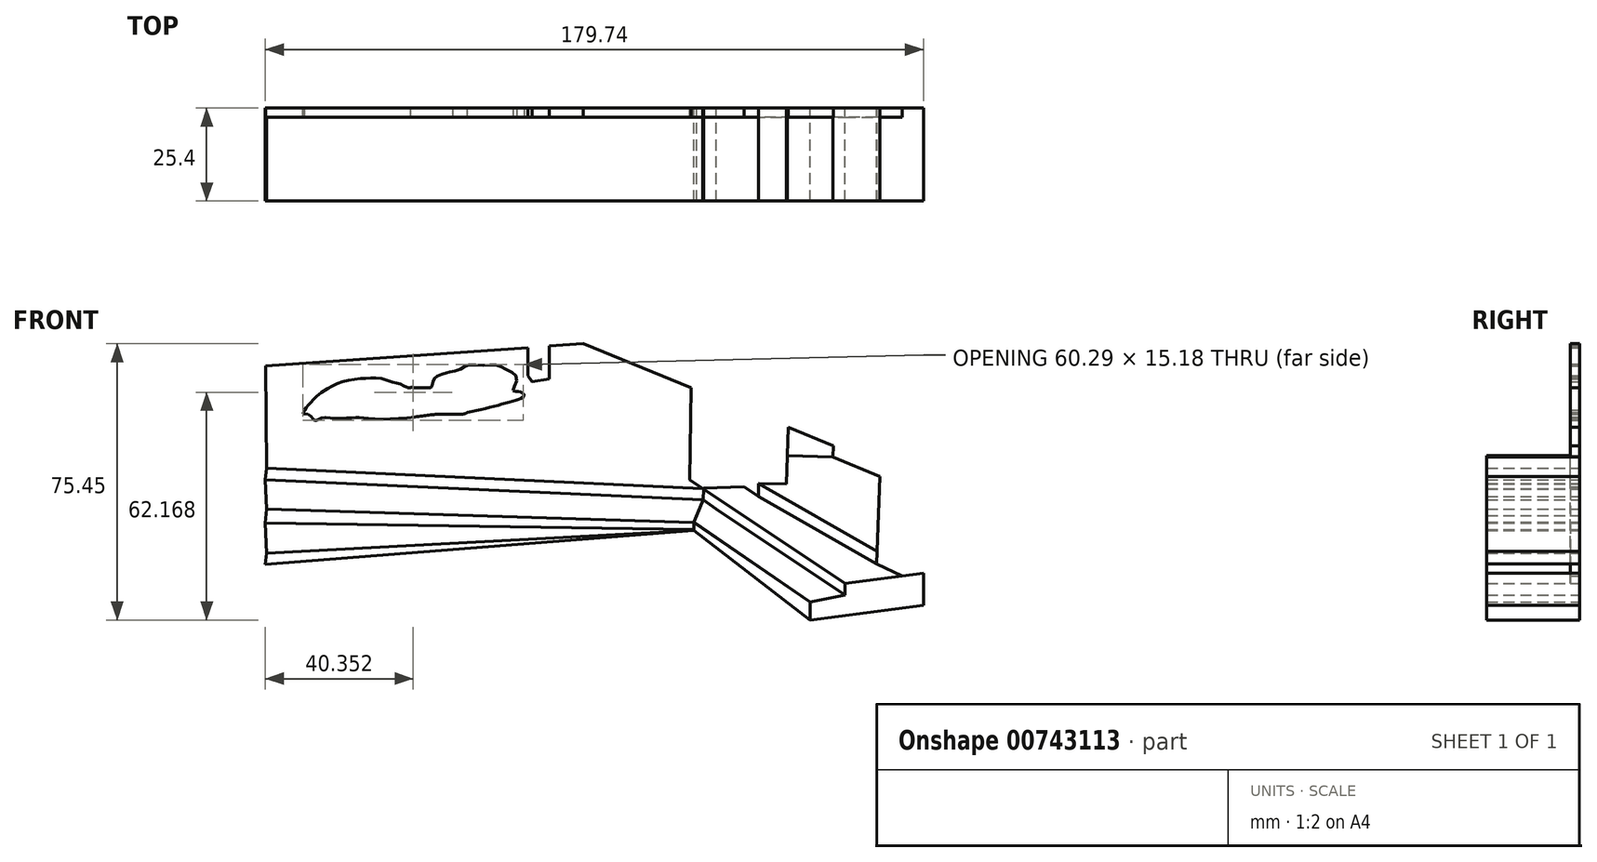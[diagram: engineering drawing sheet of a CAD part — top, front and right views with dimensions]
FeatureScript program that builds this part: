
annotation { "Feature Type Name" : "Feature", "Feature Type Description" : "" }
export const myFeature = defineFeature(function(context is Context, id is Id, definition is map)
    precondition{}
    {
        {
            var Q0;
            Q0=qCreatedBy(makeId("Front.planeOp"),FACE);
            var sketch = newSketch(context, id + "F0", { "sketchPlane" : qUnion([Q0])});
            skSolve(sketch);
        }
        {
            var Q0;
            Q0=qCreatedBy(makeId("Front.planeOp"),FACE);
            var sketch = newSketch(context, id + "F1", { "sketchPlane" : qUnion([Q0])});
            skPoint(sketch, "E0.0", {"position": v(-102.83, 77.74) * mm});
            skPoint(sketch, "E1.0", {"position": v(103.52, 77.74) * mm});
            skPoint(sketch, "E2.0", {"position": v(103.52, -77.03) * mm});
            skPoint(sketch, "E3.0", {"position": v(-102.83, -77.03) * mm});
            skLineSegment(sketch, "E4", {"start": v(-102.83, 77.74) * mm, "end": v(103.52, 77.74) * mm});
            skLineSegment(sketch, "E5", {"start": v(103.52, 77.74) * mm, "end": v(103.52, -77.03) * mm});
            skLineSegment(sketch, "E6", {"start": v(103.52, -77.03) * mm, "end": v(-102.83, -77.03) * mm});
            skLineSegment(sketch, "E7", {"start": v(-102.83, -77.03) * mm, "end": v(-102.83, 77.74) * mm});
            skLineSegment(sketch, "E8", {"start": v(43.21, -41.09) * mm, "end": v(82.08, -67.06) * mm});
            skLineSegment(sketch, "E9", {"start": v(82.08, -67.06) * mm, "end": v(97.77, -65) * mm});
            skLineSegment(sketch, "E10", {"start": v(97.77, -65) * mm, "end": v(103.52, 77.74) * mm});
            skLineSegment(sketch, "E11", {"start": v(97.77, -65) * mm, "end": v(90.72, -61.75) * mm});
            skLineSegment(sketch, "E12", {"start": v(90.72, -61.75) * mm, "end": v(96.33, 77.74) * mm});
            skLineSegment(sketch, "E13", {"start": v(95.01, 44.94) * mm, "end": v(60.47, 41.76) * mm});
            skLineSegment(sketch, "E14", {"start": v(60.47, 41.76) * mm, "end": v(58.42, -43.25) * mm});
            skLineSegment(sketch, "E15", {"start": v(66.15, -39.91) * mm, "end": v(68.3, 42.48) * mm});
            skLineSegment(sketch, "E16", {"start": v(68, 30.8) * mm, "end": v(80.72, 30.8) * mm});
            skLineSegment(sketch, "E17", {"start": v(80.72, 30.8) * mm, "end": v(78.77, -32.46) * mm});
            skLineSegment(sketch, "E18", {"start": v(78.77, -32.46) * mm, "end": v(87.41, -36.06) * mm});
            skLineSegment(sketch, "E19", {"start": v(87.41, -36.06) * mm, "end": v(89.94, 32.95) * mm});
            skLineSegment(sketch, "E20", {"start": v(89.94, 32.95) * mm, "end": v(94.53, 32.95) * mm});
            skLineSegment(sketch, "E21", {"start": v(50.64, -49.22) * mm, "end": v(82.08, -70.23) * mm});
            skLineSegment(sketch, "E22", {"start": v(82.08, -70.23) * mm, "end": v(82.08, -67.06) * mm});
            skLineSegment(sketch, "E23", {"start": v(50.64, -49.22) * mm, "end": v(46.93, -46.74) * mm});
            skLineSegment(sketch, "E24", {"start": v(45.9, 65.04) * mm, "end": v(43.36, -44.35) * mm});
            skLineSegment(sketch, "E25", {"start": v(43.21, -41.09) * mm, "end": v(54.51, -40.66) * mm});
            skLineSegment(sketch, "E26", {"start": v(54.51, -40.66) * mm, "end": v(58.42, -43.25) * mm});
            skLineSegment(sketch, "E27", {"start": v(54.51, -40.66) * mm, "end": v(57.06, 64.5) * mm});
            skLineSegment(sketch, "E28", {"start": v(45.9, 65.04) * mm, "end": v(57.06, 64.78) * mm});
            skLineSegment(sketch, "E29", {"start": v(57.06, 64.78) * mm, "end": v(57.06, 64.5) * mm});
            skLineSegment(sketch, "E30", {"start": v(57.06, 64.78) * mm, "end": v(102.77, 77.74) * mm});
            skLineSegment(sketch, "E31", {"start": v(97.77, -65) * mm, "end": v(103.52, -64.25) * mm});
            skLineSegment(sketch, "E32", {"start": v(43.13, -52.08) * mm, "end": v(43.13, -52.02) * mm});
            skLineSegment(sketch, "E33", {"start": v(82.08, -70.23) * mm, "end": v(73.38, -72.02) * mm});
            skLineSegment(sketch, "E34", {"start": v(58.5, -39.71) * mm, "end": v(90.86, -58.24) * mm});
            skLineSegment(sketch, "E35", {"start": v(58.5, -39.71) * mm, "end": v(66.15, -39.91) * mm});
            skLineSegment(sketch, "E36", {"start": v(43.21, -41.09) * mm, "end": v(39.7, -38.74) * mm});
            skLineSegment(sketch, "E37", {"start": v(39.7, -38.74) * mm, "end": v(40.84, 41.03) * mm});
            skLineSegment(sketch, "E38", {"start": v(40.84, 41.03) * mm, "end": v(-3.35, 35.9) * mm});
            skLineSegment(sketch, "E39", {"start": v(-3.35, 35.9) * mm, "end": v(-3.35, -11.94) * mm});
            skLineSegment(sketch, "E40", {"start": v(-3.35, -11.94) * mm, "end": v(1.34, -11.22) * mm});
            skLineSegment(sketch, "E41", {"start": v(1.34, -11.22) * mm, "end": v(1.34, 36.44) * mm});
            skLineSegment(sketch, "E42", {"start": v(-4.84, 49.27) * mm, "end": v(-4.49, -10.33) * mm});
            skLineSegment(sketch, "E43", {"start": v(-4.49, -10.33) * mm, "end": v(-3.35, -11.94) * mm});
            skLineSegment(sketch, "E44", {"start": v(1.34, 36.44) * mm, "end": v(25.15, 35.82) * mm});
            skLineSegment(sketch, "E45", {"start": v(25.15, 35.82) * mm, "end": v(25.15, 39.2) * mm});
            skLineSegment(sketch, "E46", {"start": v(-4.84, 49.27) * mm, "end": v(45.9, 65.04) * mm});
            skLineSegment(sketch, "E47", {"start": v(-75.94, -35.54) * mm, "end": v(-76.18, -7.57) * mm});
            skLineSegment(sketch, "E48", {"start": v(-76.18, -7.57) * mm, "end": v(-4.53, -2.63) * mm});
            skLineSegment(sketch, "E49.trimOffspring", {"start": v(1.34, -2.22) * mm, "end": v(10.65, -1.58) * mm});
            skLineSegment(sketch, "E50", {"start": v(43.21, -41.09) * mm, "end": v(-75.94, -35.54) * mm});
            skLineSegment(sketch, "E51", {"start": v(-75.94, -35.54) * mm, "end": v(-76.22, -38.74) * mm});
            skLineSegment(sketch, "E52", {"start": v(-76.22, -38.74) * mm, "end": v(43.21, -44.26) * mm});
            skLineSegment(sketch, "E53", {"start": v(40.83, -50.44) * mm, "end": v(-75.94, -46.74) * mm});
            skPoint(sketch, "E53.endSnap0", {"position": v(46.93, -46.74) * mm});
            skLineSegment(sketch, "E54", {"start": v(-75.94, -46.74) * mm, "end": v(-76.22, -50.51) * mm});
            skLineSegment(sketch, "E55", {"start": v(-76.22, -50.51) * mm, "end": v(40.83, -52.38) * mm});
            skLineSegment(sketch, "E56", {"start": v(40.83, -52.54) * mm, "end": v(-75.94, -58.86) * mm});
            skLineSegment(sketch, "E57", {"start": v(-75.94, -58.86) * mm, "end": v(-76.22, -61.88) * mm});
            skLineSegment(sketch, "E58", {"start": v(-76.22, -61.88) * mm, "end": v(40.83, -52.6) * mm});
            skLineSegment(sketch, "E59", {"start": v(-75.94, -58.86) * mm, "end": v(-76.22, -50.51) * mm});
            skLineSegment(sketch, "E60", {"start": v(-75.94, -46.74) * mm, "end": v(-76.22, -38.74) * mm});
            skLineSegment(sketch, "E61", {"start": v(-76.22, -61.88) * mm, "end": v(-76.22, -50.51) * mm});
            skLineSegment(sketch, "E62", {"start": v(-76.22, -38.74) * mm, "end": v(-76.22, -50.51) * mm});
            skLineSegment(sketch, "E63", {"start": v(-76.22, -38.74) * mm, "end": v(-76.45, -11.36) * mm});
            skLineSegment(sketch, "E64", {"start": v(-76.45, -11.36) * mm, "end": v(-76.18, -7.57) * mm});
            skLineSegment(sketch, "E65", {"start": v(90.72, -61.75) * mm, "end": v(58.42, -43.25) * mm});
            skLineSegment(sketch, "E66", {"start": v(87.41, -36.06) * mm, "end": v(91.68, -37.84) * mm});
            skLineSegment(sketch, "E67", {"start": v(103.52, -70.23) * mm, "end": v(103.52, -64.25) * mm});
            skLineSegment(sketch, "E68", {"start": v(17.54, 36.02) * mm, "end": v(17.54, -3.57) * mm});
            skLineSegment(sketch, "E69", {"start": v(17.54, -3.57) * mm, "end": v(40.07, -12.34) * mm});
            skLineSegment(sketch, "E70", {"start": v(78.77, -32.46) * mm, "end": v(66.36, -32.14) * mm});
            skLineSegment(sketch, "E71", {"start": v(78.86, -29.47) * mm, "end": v(66.56, -24.44) * mm});
            skLineSegment(sketch, "E72.trimOffspring", {"start": v(40.05, -13.6) * mm, "end": v(17.54, -4.4) * mm});
            skLineSegment(sketch, "E73.trimOffspring", {"start": v(66.6, -22.66) * mm, "end": v(78.92, -27.46) * mm});
            skLineSegment(sketch, "E74", {"start": v(17.54, -3.57) * mm, "end": v(17.54, -4.4) * mm});
            skLineSegment(sketch, "E75", {"start": v(17.54, -4.4) * mm, "end": v(10.65, -1.58) * mm});
            skFitSpline(sketch, "E76", {"points": [v(-66.01, -20.65) * mm, v(-65.13, -20.7) * mm, v(-63.54, -21.59) * mm, v(-62.6, -22.57) * mm, v(-60.78, -21.82) * mm, v(-57.56, -21.91) * mm, v(-52.75, -21.82) * mm, v(-50.41, -21.73) * mm, v(-45.84, -22.15) * mm, v(-35.4, -21.56) * mm, v(-29.46, -20.86) * mm, v(-23.95, -20.71) * mm, v(-17.04, -19.5) * mm, v(-10.69, -17.81) * mm, v(-6.95, -16.7) * mm, v(-5.55, -15.76) * mm, v(-6.2, -14.83) * mm, v(-7.89, -14.54) * mm, v(-8.54, -14.36) * mm, v(-7.7, -12.12) * mm, v(-8.17, -9.78) * mm, v(-9.94, -8.94) * mm, v(-10.6, -8.47) * mm, v(-13.21, -7.35) * mm, v(-16.85, -7.44) * mm, v(-21.34, -7.54) * mm, v(-22.83, -8.47) * mm, v(-25.64, -9.22) * mm, v(-26.94, -9.6) * mm, v(-29, -10.25) * mm, v(-30.21, -11.28) * mm, v(-30.5, -12.4) * mm, v(-30.87, -13.42) * mm, v(-30.96, -13.52) * mm, v(-31.8, -13.61) * mm, v(-33.3, -13.61) * mm, v(-35.07, -13.61) * mm, v(-35.91, -13.52) * mm, v(-36, -13.52) * mm, v(-36.47, -13.52) * mm], "startDerivative": vector(49.88, 3) * mm, "endDerivative": vector(-48.9, 0.35) * mm});
            skFitSpline(sketch, "E77", {"points": [v(-36.47, -13.52) * mm, v(-37.48, -13.52) * mm, v(-39.06, -12.71) * mm, v(-40.65, -12.3) * mm, v(-44.16, -11.17) * mm, v(-47.7, -10.98) * mm, v(-50.98, -11.17) * mm, v(-55.6, -12.1) * mm, v(-58.7, -13.52) * mm, v(-62.77, -16.39) * mm, v(-63.75, -17.6) * mm, v(-64.96, -18.77) * mm, v(-65.48, -19.7) * mm, v(-65.74, -20.64) * mm], "startDerivative": vector(-19.12, -3.26) * mm, "endDerivative": vector(-4.99, -19.18) * mm});
            skFitSpline(sketch, "E78", {"points": [v(-66.01, -20.65) * mm, v(-65.48, -19.7) * mm], "startDerivative": vector(0.54, 0.95) * mm, "endDerivative": vector(0.54, 0.95) * mm});
            skFitSpline(sketch, "E79", {"points": [v(-37.48, -13.52) * mm, v(-35.73, -14.13) * mm, v(-35.02, -14.6) * mm, v(-34.18, -15.67) * mm, v(-33.9, -16) * mm, v(-32.18, -17.35) * mm, v(-31.52, -18.05) * mm, v(-31.62, -19.13) * mm, v(-32.22, -20.06) * mm, v(-33.34, -20.86) * mm, v(-35.4, -21.56) * mm], "startDerivative": vector(16.47, -5.37) * mm, "endDerivative": vector(-16.95, -4.88) * mm});
            skFitSpline(sketch, "E80", {"points": [v(-29.46, -18.99) * mm, v(-27.64, -20.34) * mm, v(-24.93, -20.77) * mm, v(-21, -20.33) * mm, v(-19.66, -17.3) * mm, v(-19.24, -15.25) * mm, v(-21.34, -12.82) * mm, v(-23.11, -11.75) * mm, v(-25.45, -11.51) * mm, v(-27.83, -12.54) * mm, v(-28.81, -13.57) * mm, v(-28.95, -14.08) * mm, v(-29.46, -16.47) * mm, v(-29.46, -18.99) * mm]});
            skFitSpline(sketch, "E81", {"points": [v(-28.95, -14.08) * mm, v(-30.45, -15.34) * mm, v(-30.82, -16.84) * mm, v(-31.05, -18.33) * mm, v(-30.5, -19.27) * mm, v(-29.46, -18.99) * mm], "startDerivative": vector(-7.68, -4.86) * mm, "endDerivative": vector(6.36, 3.33) * mm});
            skFitSpline(sketch, "E82", {"points": [v(-30.96, -13.52) * mm, v(-30.96, -14.5) * mm, v(-30.12, -14.93) * mm], "startDerivative": vector(-0.43, -2.23) * mm, "endDerivative": vector(2.13, -0.6) * mm});
            skFitSpline(sketch, "E83", {"points": [v(-8.54, -14.36) * mm, v(-8.97, -15.25) * mm, v(-9.25, -15.67) * mm, v(-9.95, -16.7) * mm, v(-10.98, -16.7) * mm, v(-11.86, -16.7) * mm, v(-13.78, -16.7) * mm, v(-14.48, -17.68) * mm, v(-14.76, -17.82) * mm, v(-15.55, -17.91) * mm, v(-16.63, -17.96) * mm, v(-17.7, -18) * mm, v(-18.68, -17.87) * mm, v(-19.24, -17.5) * mm, v(-19.66, -17.3) * mm], "startDerivative": vector(-5.95, -13.66) * mm, "endDerivative": vector(-8.27, 2.9) * mm});
            skLineSegment(sketch, "E84", {"start": v(29.2, 30.24) * mm, "end": v(40.69, 30.24) * mm});
            skLineSegment(sketch, "E85", {"start": v(29.2, 30.24) * mm, "end": v(28.56, -7.86) * mm});
            skLineSegment(sketch, "E86", {"start": v(41.58, -48.49) * mm, "end": v(40.83, -50.44) * mm});
            skLineSegment(sketch, "E87", {"start": v(40.83, -50.44) * mm, "end": v(40.83, -52.6) * mm});
            skLineSegment(sketch, "E88", {"start": v(40.83, -52.6) * mm, "end": v(72.51, -77.03) * mm});
            skLineSegment(sketch, "E89", {"start": v(72.51, -77.03) * mm, "end": v(72.51, -73.03) * mm});
            skLineSegment(sketch, "E90", {"start": v(73.38, -72.02) * mm, "end": v(72.51, -72.2) * mm});
            skLineSegment(sketch, "E91", {"start": v(72.51, -73.03) * mm, "end": v(72.51, -72.2) * mm});
            skLineSegment(sketch, "E92", {"start": v(72.51, -72.2) * mm, "end": v(40.83, -50.44) * mm});
            skLineSegment(sketch, "E93", {"start": v(72.51, -77.03) * mm, "end": v(103.52, -72.97) * mm});
            skPoint(sketch, "E94.orphan", {"position": v(43.21, -50.51) * mm});
            skLineSegment(sketch, "E95", {"start": v(72.51, -72.2) * mm, "end": v(40.83, -50.28) * mm});
            skLineSegment(sketch, "E96", {"start": v(40.83, -50.28) * mm, "end": v(40.83, -52.6) * mm});
            skLineSegment(sketch, "E97", {"start": v(40.83, -50.28) * mm, "end": v(43.36, -44.26) * mm});
            skLineSegment(sketch, "E98", {"start": v(43.21, -44.26) * mm, "end": v(43.36, -44.26) * mm});
            skLineSegment(sketch, "E99", {"start": v(43.36, -44.26) * mm, "end": v(46.93, -46.74) * mm});
            skSolve(sketch);
        }
        {
            var Q0;
            {var subQ8=sQuery(id+"F1.wireOp",EDGE,"E36");Q0=makeQuery(id+"F1.imprint","IMPRINT",FACE,{"disambiguationData":[TD([[makeQuery(id+"F1.imprint","IMPRINT",EDGE,{"derivedFrom":subQ8}),1.0]])]});}
            var Q1;
            {var subQ0=sQuery(id+"F1.wireOp",EDGE,"E9");Q1=makeQuery(id+"F1.imprint","IMPRINT",FACE,{"disambiguationData":[TD([[makeQuery(id+"F1.imprint","IMPRINT",EDGE,{"derivedFrom":subQ0}),1.0]])]});}
            var Q2;
            {var subQ0=sQuery(id+"F1.wireOp",EDGE,"E70");Q2=makeQuery(id+"F1.imprint","IMPRINT",FACE,{"disambiguationData":[TD([[makeQuery(id+"F1.imprint","IMPRINT",EDGE,{"derivedFrom":subQ0}),-1.0]])]});}
            extrude(context, id + "F2", {"entities" : qUnion([Q0, Q1, Q2]), "depth" : 2.54 * mm, "offsetDistance" : 25.4 * mm});
        }
        {
            var Q0;
            Q0=makeQuery(id+"F1.imprint","IMPRINT",FACE,{"disambiguationData":[TD([[makeQuery(id+"F1.imprint","IMPRINT",EDGE,{"derivedFrom":sQuery(id+"F1.wireOp",EDGE,"E18")}),-1.0]])]});
            extrude(context, id + "F3", {"entities" : qUnion([Q0]), "depth" : 25.4 * mm, "offsetDistance" : 25.4 * mm});
        }
        {
            var Q0;
            {var subQ6=sQuery(id+"F1.wireOp",EDGE,"E52");Q0=makeQuery(id+"F1.imprint","IMPRINT",FACE,{"disambiguationData":[TD([[makeQuery(id+"F1.imprint","IMPRINT",EDGE,{"derivedFrom":subQ6}),-1.0]])]});}
            extrude(context, id + "F4", {"entities" : qUnion([Q0]), "depth" : 25.4 * mm, "offsetDistance" : 25.4 * mm});
        }
        {
            var Q0;
            Q0=makeQuery(id+"F1.imprint","IMPRINT",FACE,{"disambiguationData":[TD([[makeQuery(id+"F1.imprint","IMPRINT",EDGE,{"derivedFrom":sQuery(id+"F1.wireOp",EDGE,"E21")}),-1.0]])]});
            extrude(context, id + "F5", {"entities" : qUnion([Q0]), "depth" : 25.4 * mm, "offsetDistance" : 25.4 * mm});
        }
        {
            var Q0;
            {var subQ0=sQuery(id+"F1.wireOp",EDGE,"E55");Q0=makeQuery(id+"F1.imprint","IMPRINT",FACE,{"disambiguationData":[TD([[makeQuery(id+"F1.imprint","IMPRINT",EDGE,{"derivedFrom":subQ0}),-1.0]])]});}
            extrude(context, id + "F6", {"entities" : qUnion([Q0]), "depth" : 25.4 * mm, "offsetDistance" : 25.4 * mm});
        }
        {
            var Q0;
            {var subQ0=sQuery(id+"F1.wireOp",EDGE,"E56");Q0=makeQuery(id+"F1.imprint","IMPRINT",FACE,{"disambiguationData":[TD([[makeQuery(id+"F1.imprint","IMPRINT",EDGE,{"derivedFrom":subQ0}),1.0]])]});}
            var Q1;
            {var subQ0=sQuery(id+"F1.wireOp",EDGE,"E53");Q1=makeQuery(id+"F1.imprint","IMPRINT",FACE,{"disambiguationData":[TD([[makeQuery(id+"F1.imprint","IMPRINT",EDGE,{"derivedFrom":subQ0}),1.0]])]});}
            var Q2;
            {var subQ0=sQuery(id+"F1.wireOp",EDGE,"E50");Q2=makeQuery(id+"F1.imprint","IMPRINT",FACE,{"disambiguationData":[TD([[makeQuery(id+"F1.imprint","IMPRINT",EDGE,{"derivedFrom":subQ0}),1.0]])]});}
            extrude(context, id + "F7", {"entities" : qUnion([Q0, Q1, Q2]), "depth" : 25.4 * mm, "offsetDistance" : 25.4 * mm});
        }
        {
            var Q0;
            {var subQ5=sQuery(id+"F1.wireOp",EDGE,"E88");Q0=makeQuery(id+"F1.imprint","IMPRINT",FACE,{"disambiguationData":[TD([[makeQuery(id+"F1.imprint","IMPRINT",EDGE,{"derivedFrom":subQ5}),1.0]])]});}
            var Q1;
            Q1=makeQuery(id+"F1.imprint","IMPRINT",FACE,{"disambiguationData":[TD([[makeQuery(id+"F1.imprint","IMPRINT",EDGE,{"derivedFrom":sQuery(id+"F1.wireOp",EDGE,"E21")}),1.0]])]});
            var Q2;
            {var subQ2=sQuery(id+"F1.wireOp",EDGE,"E34");Q2=makeQuery(id+"F1.imprint","IMPRINT",FACE,{"disambiguationData":[TD([[makeQuery(id+"F1.imprint","IMPRINT",EDGE,{"derivedFrom":subQ2}),-1.0]])]});}
            extrude(context, id + "F8", {"entities" : qUnion([Q0, Q1, Q2]), "depth" : 25.4 * mm, "offsetDistance" : 25.4 * mm});
        }
        {
            var Q0;
            Q0=makeQuery(id+"F1.imprint","IMPRINT",FACE,{"disambiguationData":[TD([[makeQuery(id+"F1.imprint","IMPRINT",EDGE,{"derivedFrom":sQuery(id+"F1.wireOp",EDGE,"E9")}),-1.0]])]});
            extrude(context, id + "F9", {"entities" : qUnion([Q0]), "depth" : 25.4 * mm, "offsetDistance" : 25.4 * mm});
        }
    });
